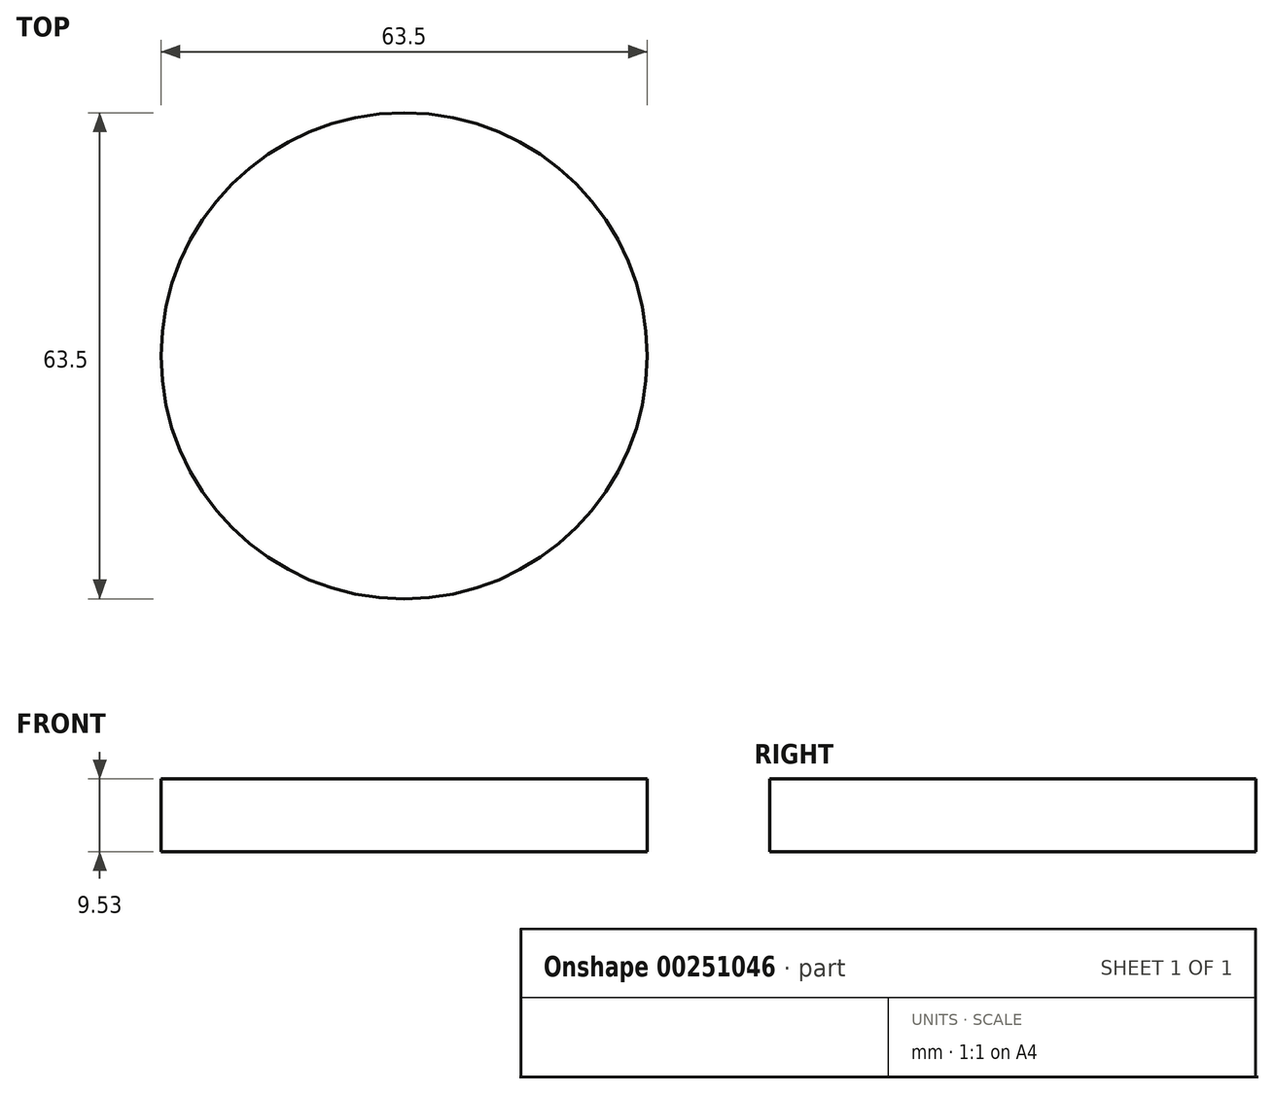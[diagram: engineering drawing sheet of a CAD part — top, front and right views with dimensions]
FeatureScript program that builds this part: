
annotation { "Feature Type Name" : "Feature", "Feature Type Description" : "" }
export const myFeature = defineFeature(function(context is Context, id is Id, definition is map)
    precondition{}
    {
        {
            var Q0;
            Q0=qCreatedBy(makeId("Top.planeOp"),FACE);
            var sketch = newSketch(context, id + "F0", { "sketchPlane" : qUnion([Q0])});
            skCircle(sketch, "E0", {"center": v(0, 0) * mm, "radius": 31.75 * mm});
            skSolve(sketch);
        }
        {
            var Q0;
            Q0=makeQuery(id+"F0.imprint","IMPRINT",FACE,{"disambiguationData":[TD([[makeQuery(id+"F0.imprint","IMPRINT",EDGE,{"derivedFrom":sQuery(id+"F0.wireOp",EDGE,"E0")}),1.0]])]});
            extrude(context, id + "F1", {"entities" : qUnion([Q0]), "depth" : 9.52 * mm});
        }
    });
